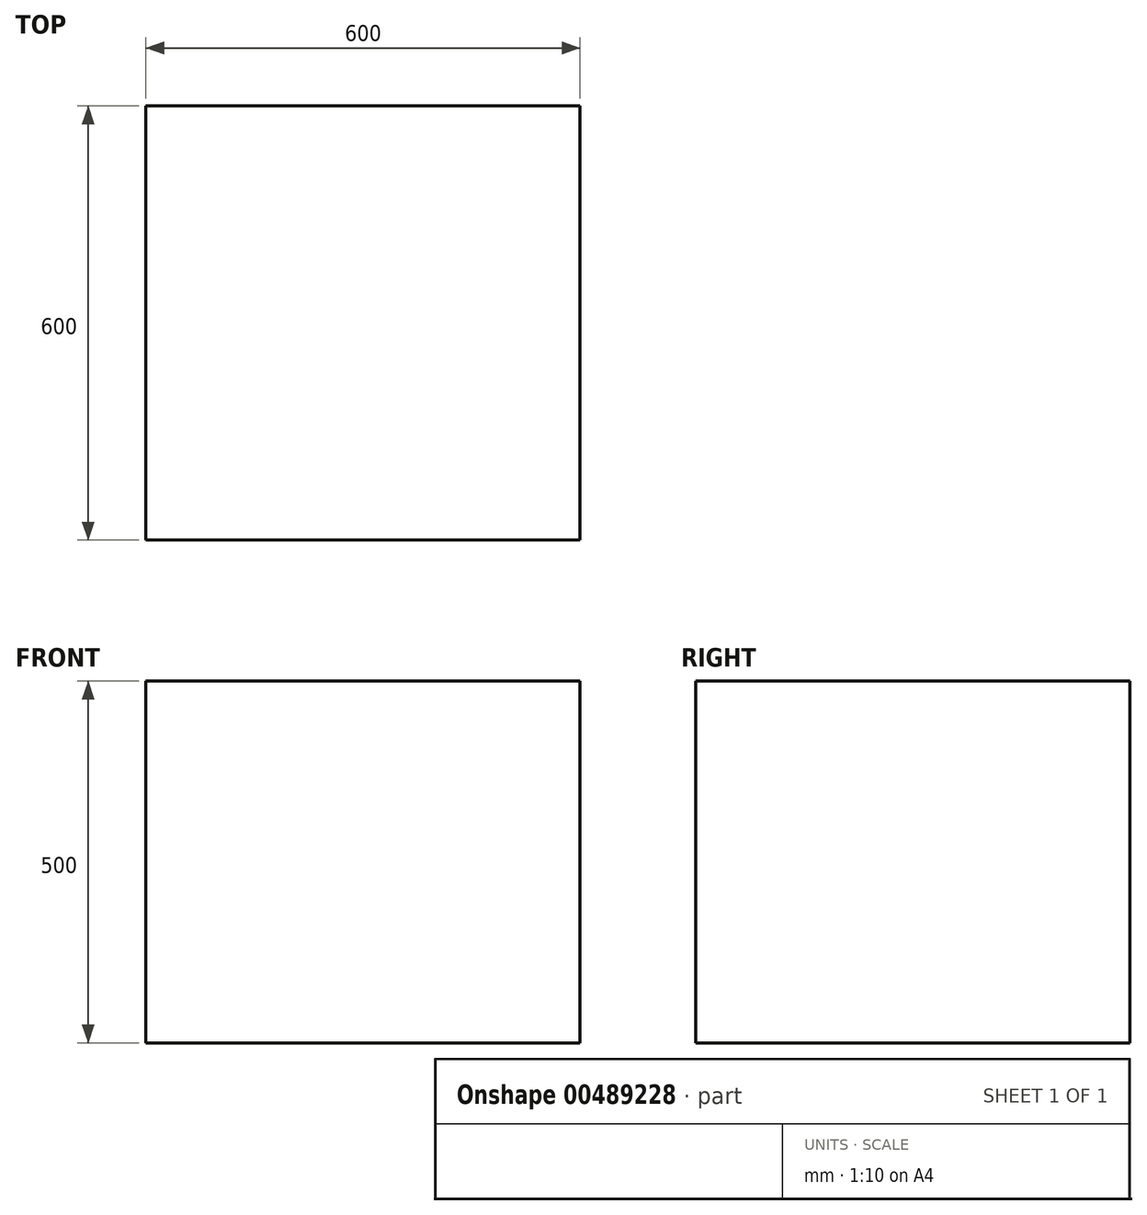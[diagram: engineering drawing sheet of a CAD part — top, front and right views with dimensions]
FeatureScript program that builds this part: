
annotation { "Feature Type Name" : "Feature", "Feature Type Description" : "" }
export const myFeature = defineFeature(function(context is Context, id is Id, definition is map)
    precondition{}
    {
        {
            var Q0;
            Q0=qCreatedBy(makeId("Front.planeOp"),FACE);
            var sketch = newSketch(context, id + "F0", { "sketchPlane" : qUnion([Q0])});
            skLineSegment(sketch, "E0.bottom", {"start": v(0, 0) * mm, "end": v(-600, 0) * mm});
            skLineSegment(sketch, "E0.top", {"start": v(0, -500) * mm, "end": v(-600, -500) * mm});
            skLineSegment(sketch, "E0.left", {"start": v(0, 0) * mm, "end": v(0, -500) * mm});
            skLineSegment(sketch, "E0.right", {"start": v(-600, 0) * mm, "end": v(-600, -500) * mm});
            skSolve(sketch);
        }
        {
            var Q0;
            Q0=makeQuery(id+"F0.imprint","IMPRINT",FACE,{"disambiguationData":[TD([[makeQuery(id+"F0.imprint","IMPRINT",EDGE,{"derivedFrom":sQuery(id+"F0.wireOp",EDGE,"E0.bottom")}),1.0]])]});
            extrude(context, id + "F1", {"entities" : qUnion([Q0]), "oppositeDirection" : true, "depth" : 600 * mm});
        }
    });
